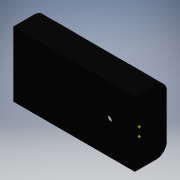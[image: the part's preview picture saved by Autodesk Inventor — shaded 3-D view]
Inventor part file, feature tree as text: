
AUTODESK INVENTOR PART (.ipt)
format: ipt  version: 2016 (Build 200138000, 138)  size: 192,512 bytes
history: native  units: mm
features: sketch x8, extrude x5, other x2, fillet x1, hole x1, pattern_circular x1, projected_geometry x1
ambient origin geometry x8: Origin, YZ Plane, XZ Plane, XY Plane, X Axis, Y Axis, Z Axis, Center Point
bodies: Solid1 (feature_tree)
feature tree (19):
  extrude  "Extrusion1"  Depth=30.5mm
  fillet  "Fillet1"  [1 undecoded]
  extrude  "Extrusion2"  Depth=57.2mm TaperAngle=0.0deg
  extrude  "Extrusion3"  Depth=1.0mm
  hole  "Hole1"  [1 undecoded]
  extrude  "Extrusion4"  Depth=1.0mm
  pattern_circular  "Circular Pattern1"  [2 undecoded]
  extrude  "Extrusion5"  Depth=55.2mm TaperAngle=0.0deg
  sketch  "Sketch7"  dims[d14=10.0mm]
  other  "red"
  sketch  "Sketch8"  dims[d15=5.0mm d16=3.0mm d17=55.2mm d18=0.0mm d19=32.7mm d20=16.35mm d21=14.25mm d22=14.25mm d23=14.25mm d24=2.7mm d25=6.0mm d26=4.0mm d27=2.0mm d28=90.0deg d29=8.0mm d30=20.594885mm d31=7.2mm d32=7.2mm d33=1.0mm d34=0.0mm d35=20.0mm d36=360.0deg d38=2.0mm d39=2.0mm d40=2.0mm d41=2.0mm d42=0.5mm d43=0.0mm]
  other  "blk"
  sketch  "Sketch1"  dims[d0=15.0mm d1=30.5mm d2=0.0mm]
  sketch  "Sketch2"  dims[d3=0.0mm d4=57.2mm d5=0.0mm]
  projected_geometry  "Projected Loop1"
  sketch  "Sketch3"  dims[d6=5.0mm d7=1.0mm]
  sketch  "Sketch4"  dims[d8=55.2mm d9=0.0mm d10=1.0mm]
  sketch  "Sketch5"  dims[d11=1.0mm d12=1.0mm]
  sketch  "Sketch6"  dims[d13=1.0mm]
note: 4 required parameter values undecoded (feature->parameter linkage not recoverable at this tier; creation-order binding heuristic only, values carry confidence <= 0.55)
